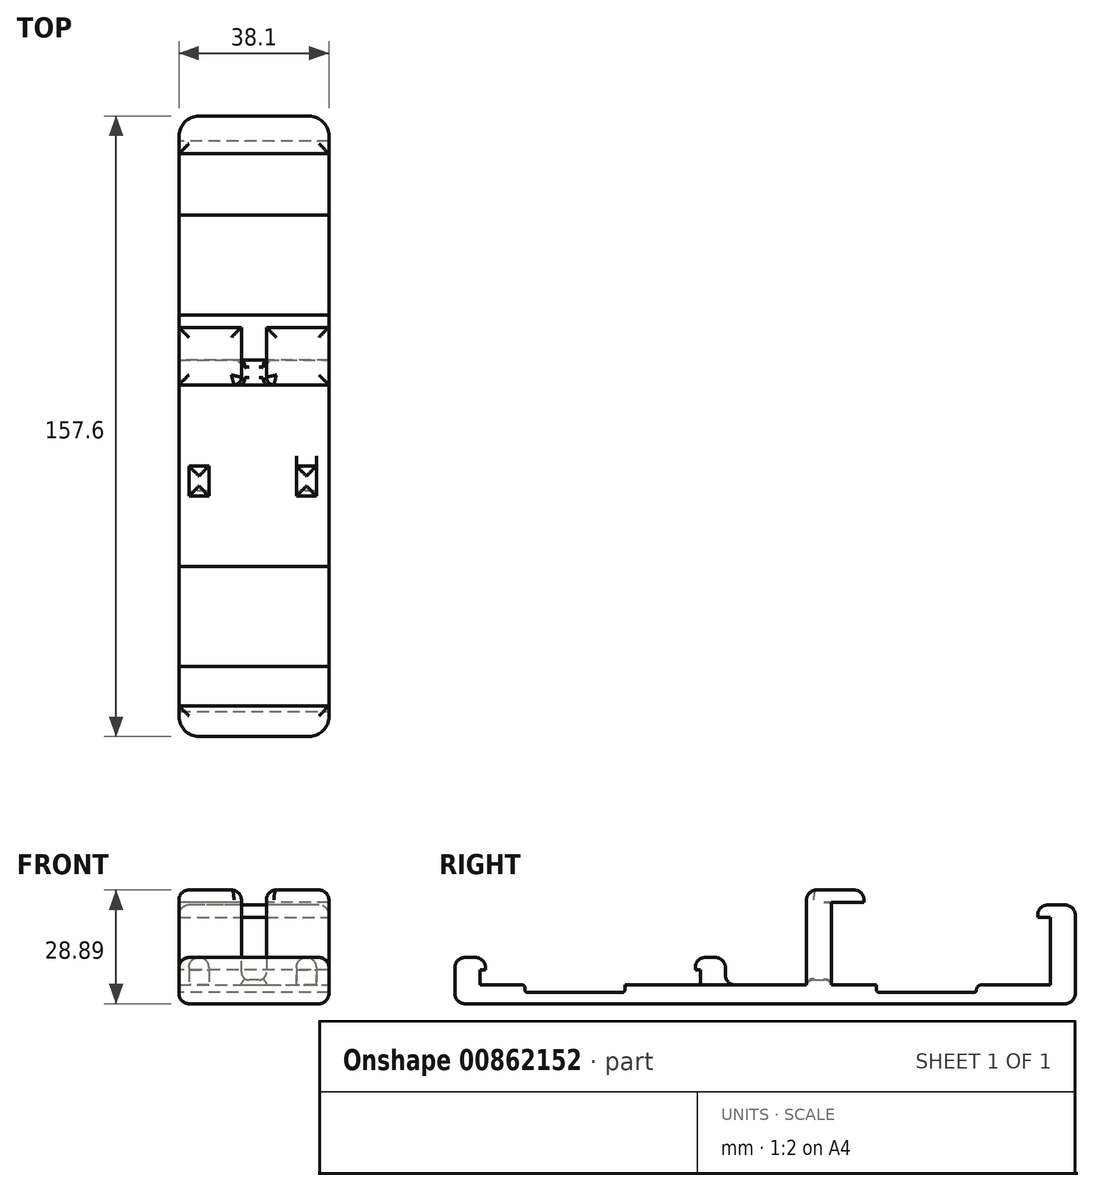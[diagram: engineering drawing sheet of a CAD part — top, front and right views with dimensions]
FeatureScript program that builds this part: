
annotation { "Feature Type Name" : "Feature", "Feature Type Description" : "" }
export const myFeature = defineFeature(function(context is Context, id is Id, definition is map)
    precondition{}
    {
        {
            var Q0;
            Q0=qCreatedBy(makeId("Top.planeOp"),FACE);
            var sketch = newSketch(context, id + "F0", { "sketchPlane" : qUnion([Q0])});
            skLineSegment(sketch, "E0.bottom", {"start": v(0, 0) * mm, "end": v(88, 0) * mm, "construction": true});
            skLineSegment(sketch, "E0.top", {"start": v(0, 56) * mm, "end": v(88, 56) * mm, "construction": true});
            skLineSegment(sketch, "E0.left", {"start": v(0, 0) * mm, "end": v(0, 56) * mm, "construction": true});
            skLineSegment(sketch, "E0.right", {"start": v(88, 0) * mm, "end": v(88, 56) * mm, "construction": true});
            skLineSegment(sketch, "E1.bottom", {"start": v(12.26, -6.35) * mm, "end": v(50.36, -6.35) * mm});
            skLineSegment(sketch, "E1.top", {"start": v(12.26, 62.35) * mm, "end": v(50.36, 62.35) * mm});
            skLineSegment(sketch, "E1.left", {"start": v(12.26, -6.35) * mm, "end": v(12.26, 62.35) * mm});
            skLineSegment(sketch, "E1.right", {"start": v(50.36, -6.35) * mm, "end": v(50.36, 62.35) * mm});
            skSolve(sketch);
        }
        {
            var Q0;
            Q0 = qSketchRegion(id + "F0", true);
            extrude(context, id + "F1", {"entities" : qUnion([Q0]), "depth" : 4.76 * mm, "offsetDistance" : 25.4 * mm});
        }
        {
            var Q0;
            Q0=makeQuery(id+"F1.opExtrude","CAP_FACE",FACE,{"disambiguationData":[OSD([sQuery(id+"F0.wireOp",EDGE,"E1.bottom"),sQuery(id+"F0.wireOp",EDGE,"E1.top"),sQuery(id+"F0.wireOp",EDGE,"E1.left"),sQuery(id+"F0.wireOp",EDGE,"E1.right")])],"isStart":false});
            var sketch = newSketch(context, id + "F2", { "sketchPlane" : qUnion([Q0])});
            skLineSegment(sketch, "E2.bottom", {"start": v(12.26, -6.35) * mm, "end": v(50.36, -6.35) * mm});
            skLineSegment(sketch, "E2.top", {"start": v(12.26, 0) * mm, "end": v(50.36, 0) * mm});
            skLineSegment(sketch, "E2.left", {"start": v(12.26, -6.35) * mm, "end": v(12.26, 0) * mm});
            skLineSegment(sketch, "E2.right", {"start": v(50.36, -6.35) * mm, "end": v(50.36, 0) * mm});
            skLineSegment(sketch, "E3.bottom", {"start": v(19.88, 56) * mm, "end": v(14.8, 56) * mm});
            skLineSegment(sketch, "E3.top", {"start": v(19.88, 62.35) * mm, "end": v(14.8, 62.35) * mm});
            skLineSegment(sketch, "E3.left", {"start": v(19.88, 56) * mm, "end": v(19.88, 62.35) * mm});
            skLineSegment(sketch, "E3.right", {"start": v(14.8, 56) * mm, "end": v(14.8, 62.35) * mm});
            skLineSegment(sketch, "E4.1.0.0", {"start": v(47.18, 56) * mm, "end": v(42.1, 56) * mm});
            skLineSegment(sketch, "E4.1.0.1", {"start": v(42.1, 56) * mm, "end": v(42.1, 62.35) * mm});
            skLineSegment(sketch, "E4.1.0.2", {"start": v(47.18, 56) * mm, "end": v(47.18, 62.35) * mm});
            skLineSegment(sketch, "E4.1.0.3", {"start": v(47.18, 62.35) * mm, "end": v(42.1, 62.35) * mm});
            skLineSegment(sketch, "E4.direction1", {"start": v(14.8, 56) * mm, "end": v(42.1, 56) * mm, "construction": true});
            skSolve(sketch);
        }
        {
            var Q0;
            Q0 = qSketchRegion(id + "F2", true);
            extrude(context, id + "F3", {"entities" : qUnion([Q0]), "operationType" : NewBodyOperationType.ADD, "depth" : 7 * mm, "offsetDistance" : 25.4 * mm});
        }
        {
            var Q0;
            Q0=makeQuery(id+"F3.opExtrude","SWEPT_FACE",FACE,{"disambiguationData":[OSD([sQuery(id+"F2.wireOp",EDGE,"E3.bottom")])]});
            var sketch = newSketch(context, id + "F4", { "sketchPlane" : qUnion([Q0])});
            skLineSegment(sketch, "E5.bottom", {"start": v(12.26, 11.75) * mm, "end": v(46.53, 11.75) * mm, "construction": true});
            skLineSegment(sketch, "E5.top", {"start": v(12.26, 8.57) * mm, "end": v(46.53, 8.57) * mm, "construction": true});
            skLineSegment(sketch, "E5.left", {"start": v(12.26, 11.75) * mm, "end": v(12.26, 8.57) * mm, "construction": true});
            skLineSegment(sketch, "E5.right", {"start": v(46.53, 11.75) * mm, "end": v(46.53, 8.57) * mm, "construction": true});
            skLineSegment(sketch, "E6.bottom", {"start": v(14.8, 11.75) * mm, "end": v(19.88, 11.75) * mm});
            skLineSegment(sketch, "E6.top", {"start": v(14.8, 8.57) * mm, "end": v(19.88, 8.57) * mm});
            skLineSegment(sketch, "E6.left", {"start": v(14.8, 11.75) * mm, "end": v(14.8, 8.57) * mm});
            skLineSegment(sketch, "E6.right", {"start": v(19.88, 11.75) * mm, "end": v(19.88, 8.57) * mm});
            skLineSegment(sketch, "E7.1.0.0", {"start": v(42.1, 11.75) * mm, "end": v(42.1, 8.57) * mm});
            skLineSegment(sketch, "E7.1.0.1", {"start": v(39.56, 11.75) * mm, "end": v(73.84, 11.75) * mm, "construction": true});
            skLineSegment(sketch, "E7.1.0.2", {"start": v(39.56, 11.75) * mm, "end": v(39.56, 8.57) * mm, "construction": true});
            skLineSegment(sketch, "E7.1.0.3", {"start": v(39.56, 8.57) * mm, "end": v(73.84, 8.57) * mm, "construction": true});
            skLineSegment(sketch, "E7.1.0.4", {"start": v(47.18, 11.75) * mm, "end": v(47.18, 8.57) * mm});
            skLineSegment(sketch, "E7.1.0.5", {"start": v(42.1, 8.57) * mm, "end": v(47.18, 8.57) * mm});
            skLineSegment(sketch, "E7.1.0.6", {"start": v(42.1, 11.75) * mm, "end": v(47.18, 11.75) * mm});
            skLineSegment(sketch, "E7.direction1", {"start": v(12.26, 8.57) * mm, "end": v(39.56, 8.57) * mm, "construction": true});
            skSolve(sketch);
        }
        {
            var Q0;
            Q0 = qSketchRegion(id + "F4", true);
            extrude(context, id + "F5", {"entities" : qUnion([Q0]), "operationType" : NewBodyOperationType.ADD, "depth" : 1.27 * mm, "offsetDistance" : 25.4 * mm});
        }
        {
            var Q0;
            Q0=makeQuery(id+"F3.opExtrude","SWEPT_FACE",FACE,{"disambiguationData":[OSD([sQuery(id+"F2.wireOp",EDGE,"E2.top")])]});
            var sketch = newSketch(context, id + "F6", { "sketchPlane" : qUnion([Q0])});
            skLineSegment(sketch, "E8.bottom", {"start": v(-50.36, 11.75) * mm, "end": v(-12.26, 11.75) * mm});
            skLineSegment(sketch, "E8.top", {"start": v(-50.36, 8.57) * mm, "end": v(-12.26, 8.57) * mm});
            skLineSegment(sketch, "E8.left", {"start": v(-50.36, 11.75) * mm, "end": v(-50.36, 8.57) * mm});
            skLineSegment(sketch, "E8.right", {"start": v(-12.26, 11.75) * mm, "end": v(-12.26, 8.57) * mm});
            skSolve(sketch);
        }
        {
            var Q0;
            Q0 = qSketchRegion(id + "F6", true);
            extrude(context, id + "F7", {"entities" : qUnion([Q0]), "operationType" : NewBodyOperationType.ADD, "depth" : 1.4 * mm, "offsetDistance" : 25.4 * mm});
        }
        {
            var Q0;
            Q0=makeQuery(id+"F3.boolean.opBoolean","MERGE",FACE,{"derivedFrom":[makeQuery(id+"F1.opExtrude","SWEPT_FACE",FACE,{"disambiguationData":[OSD([sQuery(id+"F0.wireOp",EDGE,"E1.top")])]}),makeQuery(id+"F3.opExtrude","SWEPT_FACE",FACE,{"disambiguationData":[OSD([sQuery(id+"F2.wireOp",EDGE,"bA279OWE-RNau-AAjO-aDuQ-ZZpBOvPAffWd.bottom")])]})]});
            var sketch = newSketch(context, id + "F8", { "sketchPlane" : qUnion([Q0])});
            skLineSegment(sketch, "E9.bottom", {"start": v(-50.36, 0) * mm, "end": v(-12.26, 0) * mm});
            skLineSegment(sketch, "E9.top", {"start": v(-50.36, 4.76) * mm, "end": v(-12.26, 4.76) * mm});
            skLineSegment(sketch, "E9.left", {"start": v(-50.36, 0) * mm, "end": v(-50.36, 4.76) * mm});
            skLineSegment(sketch, "E9.right", {"start": v(-12.26, 0) * mm, "end": v(-12.26, 4.76) * mm});
            skSolve(sketch);
        }
        {
            var Q0;
            Q0 = qSketchRegion(id + "F8", true);
            extrude(context, id + "F9", {"entities" : qUnion([Q0]), "operationType" : NewBodyOperationType.ADD, "depth" : 88.9 * mm, "offsetDistance" : 25.4 * mm});
        }
        {
            var Q0;
            Q0=makeQuery(id+"F9.opExtrude","SWEPT_FACE",FACE,{"disambiguationData":[OSD([sQuery(id+"F8.wireOp",EDGE,"E9.top")])]});
            var sketch = newSketch(context, id + "F10", { "sketchPlane" : qUnion([Q0])});
            skLineSegment(sketch, "E10.bottom", {"start": v(12.26, 89.34) * mm, "end": v(50.36, 89.34) * mm});
            skLineSegment(sketch, "E10.top", {"start": v(12.26, 82.99) * mm, "end": v(50.36, 82.99) * mm});
            skLineSegment(sketch, "E10.left", {"start": v(12.26, 89.34) * mm, "end": v(12.26, 82.99) * mm});
            skLineSegment(sketch, "E10.right", {"start": v(50.36, 89.34) * mm, "end": v(50.36, 82.99) * mm});
            skSolve(sketch);
        }
        {
            var Q0;
            Q0 = qSketchRegion(id + "F10", true);
            extrude(context, id + "F11", {"entities" : qUnion([Q0]), "operationType" : NewBodyOperationType.ADD, "depth" : 24.13 * mm, "offsetDistance" : 25.4 * mm});
        }
        {
            var Q0;
            {var subQ1=sQuery(id+"F10.wireOp",EDGE,"E10.bottom");Q0=makeQuery(id+"F15.boolean.opBoolean","SPLIT",FACE,{"disambiguationData":[TD([makeQuery(id+"F1.opExtrude","SWEPT_FACE",FACE,{"disambiguationData":[OSD([sQuery(id+"F0.wireOp",EDGE,"E1.right")])]})])],"derivedFrom":makeQuery(id+"F11.opExtrude","SWEPT_FACE",FACE,{"disambiguationData":[OSD([subQ1])]})});}
            var sketch = newSketch(context, id + "F12", { "sketchPlane" : qUnion([Q0])});
            skLineSegment(sketch, "E11.bottom", {"start": v(-50.36, 28.9) * mm, "end": v(-12.26, 28.9) * mm});
            skLineSegment(sketch, "E11.top", {"start": v(-50.36, 25.72) * mm, "end": v(-12.26, 25.72) * mm});
            skLineSegment(sketch, "E11.left", {"start": v(-50.36, 28.9) * mm, "end": v(-50.36, 25.72) * mm});
            skLineSegment(sketch, "E11.right", {"start": v(-12.26, 28.9) * mm, "end": v(-12.26, 25.72) * mm});
            skSolve(sketch);
        }
        {
            var Q0;
            Q0=makeQuery(id+"F11.opExtrude","CAP_FACE",FACE,{"disambiguationData":[OSD([sQuery(id+"F10.wireOp",EDGE,"E10.bottom"),sQuery(id+"F10.wireOp",EDGE,"E10.top"),sQuery(id+"F10.wireOp",EDGE,"E10.left"),sQuery(id+"F10.wireOp",EDGE,"E10.right")])],"isStart":false});
            var sketch = newSketch(context, id + "F13", { "sketchPlane" : qUnion([Q0])});
            skLineSegment(sketch, "E12.bottom", {"start": v(34.48, 99.5) * mm, "end": v(28.13, 99.5) * mm});
            skLineSegment(sketch, "E12.top", {"start": v(51.97, 74.1) * mm, "end": v(28.13, 74.1) * mm});
            skLineSegment(sketch, "E13", {"start": v(28.13, 99.5) * mm, "end": v(28.13, 74.1) * mm});
            skLineSegment(sketch, "E14", {"start": v(51.97, 74.1) * mm, "end": v(51.97, 80.45) * mm});
            skLineSegment(sketch, "E15", {"start": v(51.97, 80.45) * mm, "end": v(34.48, 80.45) * mm});
            skLineSegment(sketch, "E16", {"start": v(34.48, 80.45) * mm, "end": v(34.48, 99.5) * mm});
            skSolve(sketch);
        }
        {
            var Q0;
            Q0 = qSketchRegion(id + "F12", true);
            extrude(context, id + "F14", {"entities" : qUnion([Q0]), "operationType" : NewBodyOperationType.ADD, "depth" : 8.25 * mm, "offsetDistance" : 25.4 * mm});
        }
        {
            var Q0;
            {var subQ0=sQuery(id+"F13.wireOp",EDGE,"E13");var subQ1=makeQuery(id+"F11.opExtrude","CAP_EDGE",EDGE,{"disambiguationData":[OSD([sQuery(id+"F10.wireOp",EDGE,"E10.bottom")])],"isStart":false});var subQ2=makeQuery(id+"F13.imprint","INTERSECT",VERTEX,{"derivedFrom":[subQ1,subQ0]});Q0=makeQuery(id+"F13.imprint","IMPRINT",FACE,{"disambiguationData":[TD([[makeQuery(id+"F13.imprint","IMPRINT",EDGE,{"disambiguationData":[TD([[subQ2,-1.0]])],"derivedFrom":subQ0}),1.0]])]});}
            var Q1;
            {var subQ0=sQuery(id+"F13.wireOp",EDGE,"E12.bottom");Q1=makeQuery(id+"F13.imprint","IMPRINT",FACE,{"disambiguationData":[TD([[makeQuery(id+"F13.imprint","IMPRINT",EDGE,{"derivedFrom":subQ0}),1.0]])]});}
            var Q2;
            {var subQ1=sQuery(id+"F13.wireOp",EDGE,"E12.top");Q2=makeQuery(id+"F13.imprint","IMPRINT",FACE,{"disambiguationData":[TD([[makeQuery(id+"F13.imprint","IMPRINT",EDGE,{"derivedFrom":subQ1}),-1.0]])]});}
            extrude(context, id + "F15", {"entities" : qUnion([Q0, Q1, Q2]), "operationType" : NewBodyOperationType.REMOVE, "oppositeDirection" : true, "depth" : 22.86 * mm, "offsetDistance" : 25.4 * mm});
        }
        {
            var Q0;
            {var subQ0=sQuery(id+"F8.wireOp",EDGE,"E9.left");var subQ3=sQuery(id+"F8.wireOp",EDGE,"E9.top");Q0=makeQuery(id+"F22.boolean.opBoolean","SPLIT",FACE,{"disambiguationData":[TD([makeQuery(id+"F24.opFillet","BLEND_FACE",FACE,{"disambiguationData":[OSD([subQ0])]})])],"derivedFrom":makeQuery(id+"F11.boolean.opBoolean","SPLIT",FACE,{"disambiguationData":[TD([makeQuery(id+"F11.opExtrude","SWEPT_FACE",FACE,{"disambiguationData":[OSD([sQuery(id+"F10.wireOp",EDGE,"E10.bottom")])]})])],"derivedFrom":makeQuery(id+"F9.opExtrude","SWEPT_FACE",FACE,{"disambiguationData":[OSD([subQ3])]})})});}
            var sketch = newSketch(context, id + "F16", { "sketchPlane" : qUnion([Q0])});
            skLineSegment(sketch, "E17.bottom", {"start": v(50.36, 144.9) * mm, "end": v(12.26, 144.9) * mm});
            skLineSegment(sketch, "E17.top", {"start": v(50.36, 151.25) * mm, "end": v(12.26, 151.25) * mm});
            skLineSegment(sketch, "E17.left", {"start": v(50.36, 144.9) * mm, "end": v(50.36, 151.25) * mm});
            skLineSegment(sketch, "E17.right", {"start": v(12.26, 144.9) * mm, "end": v(12.26, 151.25) * mm});
            skSolve(sketch);
        }
        {
            var Q0;
            Q0 = qSketchRegion(id + "F16", true);
            extrude(context, id + "F17", {"entities" : qUnion([Q0]), "operationType" : NewBodyOperationType.ADD, "depth" : 20.32 * mm, "offsetDistance" : 25.4 * mm});
        }
        {
            var Q0;
            Q0=makeQuery(id+"F17.opExtrude","SWEPT_FACE",FACE,{"disambiguationData":[OSD([sQuery(id+"F16.wireOp",EDGE,"E17.bottom")])]});
            var sketch = newSketch(context, id + "F18", { "sketchPlane" : qUnion([Q0])});
            skLineSegment(sketch, "E18.bottom", {"start": v(12.26, 25.08) * mm, "end": v(50.36, 25.08) * mm});
            skLineSegment(sketch, "E18.top", {"start": v(12.26, 21.9) * mm, "end": v(50.36, 21.9) * mm});
            skLineSegment(sketch, "E18.left", {"start": v(12.26, 25.08) * mm, "end": v(12.26, 21.9) * mm});
            skLineSegment(sketch, "E18.right", {"start": v(50.36, 25.08) * mm, "end": v(50.36, 21.9) * mm});
            skSolve(sketch);
        }
        {
            var Q0;
            Q0 = qSketchRegion(id + "F18", true);
            extrude(context, id + "F19", {"entities" : qUnion([Q0]), "operationType" : NewBodyOperationType.ADD, "depth" : 3.17 * mm, "offsetDistance" : 25.4 * mm});
        }
        {
            var Q0;
            Q0=makeQuery(id+"F7.boolean.opBoolean","MERGE",FACE,{"derivedFrom":[makeQuery(id+"F3.opExtrude","CAP_FACE",FACE,{"disambiguationData":[OSD([sQuery(id+"F2.wireOp",EDGE,"E2.bottom"),sQuery(id+"F2.wireOp",EDGE,"E2.top"),sQuery(id+"F2.wireOp",EDGE,"E2.left"),sQuery(id+"F2.wireOp",EDGE,"E2.right")])],"isStart":false}),makeQuery(id+"F7.opExtrude","SWEPT_FACE",FACE,{"disambiguationData":[OSD([sQuery(id+"F6.wireOp",EDGE,"E8.bottom")])]})]});
            var Q1;
            Q1=makeQuery(id+"F5.boolean.opBoolean","MERGE",FACE,{"derivedFrom":[makeQuery(id+"F3.opExtrude","CAP_FACE",FACE,{"disambiguationData":[OSD([sQuery(id+"F2.wireOp",EDGE,"bA279OWE-RNau-AAjO-aDuQ-ZZpBOvPAffWd.bottom"),sQuery(id+"F2.wireOp",EDGE,"bA279OWE-RNau-AAjO-aDuQ-ZZpBOvPAffWd.top"),sQuery(id+"F2.wireOp",EDGE,"bA279OWE-RNau-AAjO-aDuQ-ZZpBOvPAffWd.left"),sQuery(id+"F2.wireOp",EDGE,"bA279OWE-RNau-AAjO-aDuQ-ZZpBOvPAffWd.right")])],"isStart":false}),makeQuery(id+"F5.opExtrude","SWEPT_FACE",FACE,{"disambiguationData":[OSD([sQuery(id+"F4.wireOp",EDGE,"E5.bottom")])]})]});
            var Q2;
            {var subQ1=sQuery(id+"F12.wireOp",EDGE,"E11.bottom");var subQ2=sQuery(id+"F10.wireOp",EDGE,"E10.left");var subQ3=sQuery(id+"F10.wireOp",EDGE,"E10.top");Q2=makeQuery(id+"F15.boolean.opBoolean","SPLIT",FACE,{"disambiguationData":[TD([makeQuery(id+"F1.opExtrude","SWEPT_FACE",FACE,{"disambiguationData":[OSD([sQuery(id+"F0.wireOp",EDGE,"E1.left")])]})])],"derivedFrom":makeQuery(id+"F14.boolean.opBoolean","MERGE",FACE,{"derivedFrom":[makeQuery(id+"F11.opExtrude","CAP_FACE",FACE,{"disambiguationData":[OSD([sQuery(id+"F10.wireOp",EDGE,"E10.bottom"),subQ3,subQ2,sQuery(id+"F10.wireOp",EDGE,"E10.right")])],"isStart":false}),makeQuery(id+"F14.opExtrude","SWEPT_FACE",FACE,{"disambiguationData":[OSD([subQ1])]})]})});}
            var Q3;
            {var subQ0=sQuery(id+"F10.wireOp",EDGE,"E10.right");var subQ1=sQuery(id+"F10.wireOp",EDGE,"E10.top");var subQ3=sQuery(id+"F12.wireOp",EDGE,"E11.bottom");Q3=makeQuery(id+"F15.boolean.opBoolean","SPLIT",FACE,{"disambiguationData":[TD([makeQuery(id+"F1.opExtrude","SWEPT_FACE",FACE,{"disambiguationData":[OSD([sQuery(id+"F0.wireOp",EDGE,"E1.right")])]})])],"derivedFrom":makeQuery(id+"F14.boolean.opBoolean","MERGE",FACE,{"derivedFrom":[makeQuery(id+"F11.opExtrude","CAP_FACE",FACE,{"disambiguationData":[OSD([sQuery(id+"F10.wireOp",EDGE,"E10.bottom"),subQ1,sQuery(id+"F10.wireOp",EDGE,"E10.left"),subQ0])],"isStart":false}),makeQuery(id+"F14.opExtrude","SWEPT_FACE",FACE,{"disambiguationData":[OSD([subQ3])]})]})});}
            var Q4;
            Q4=makeQuery(id+"F9.boolean.opBoolean","MERGE",FACE,{"derivedFrom":[makeQuery(id+"F1.opExtrude","CAP_FACE",FACE,{"disambiguationData":[OSD([sQuery(id+"F0.wireOp",EDGE,"E1.bottom"),sQuery(id+"F0.wireOp",EDGE,"E1.top"),sQuery(id+"F0.wireOp",EDGE,"E1.left"),sQuery(id+"F0.wireOp",EDGE,"E1.right")])],"isStart":true}),makeQuery(id+"F9.opExtrude","SWEPT_FACE",FACE,{"disambiguationData":[OSD([sQuery(id+"F8.wireOp",EDGE,"E9.bottom")])]})]});
            var Q5;
            Q5=makeQuery(id+"F15.boolean.opBoolean","COPY",EDGE,{"derivedFrom":makeQuery(id+"F15.opExtrude","SWEPT_EDGE",EDGE,{"disambiguationData":[OSD([sQuery(id+"F13.wireOp",EDGE,"E13"),sQuery(id+"F13.wireOp",EDGE,"QISQvM3N-z2vj-XqKH-QPA1-7KimYQfk3j7Q")])]})});
            var Q6;
            Q6=makeQuery(id+"F15.boolean.opBoolean","COPY",EDGE,{"derivedFrom":makeQuery(id+"F15.opExtrude","SWEPT_EDGE",EDGE,{"disambiguationData":[OSD([sQuery(id+"F13.wireOp",EDGE,"E12.top"),sQuery(id+"F13.wireOp",EDGE,"E12.right")])]})});
            var Q7;
            Q7=makeQuery(id+"F19.boolean.opBoolean","MERGE",FACE,{"derivedFrom":[makeQuery(id+"F11.opExtrude","CAP_FACE",FACE,{"disambiguationData":[OSD([sQuery(id+"F10.wireOp",EDGE,"fdR43w3e-D3ww-igFy-iP3o-ReilXkbukFnq.bottom"),sQuery(id+"F10.wireOp",EDGE,"fdR43w3e-D3ww-igFy-iP3o-ReilXkbukFnq.top"),sQuery(id+"F10.wireOp",EDGE,"fdR43w3e-D3ww-igFy-iP3o-ReilXkbukFnq.left"),sQuery(id+"F10.wireOp",EDGE,"fdR43w3e-D3ww-igFy-iP3o-ReilXkbukFnq.right")])],"isStart":false}),makeQuery(id+"F19.opExtrude","SWEPT_FACE",FACE,{"disambiguationData":[OSD([sQuery(id+"F18.wireOp",EDGE,"Ol4su5Gu-75hp-AgvY-yYLj-UDWePbQuPs0d.bottom")])]})]});
            var Q8;
            Q8=makeQuery(id+"F19.boolean.opBoolean","MERGE",FACE,{"derivedFrom":[makeQuery(id+"F17.opExtrude","CAP_FACE",FACE,{"disambiguationData":[OSD([sQuery(id+"F16.wireOp",EDGE,"E17.bottom"),sQuery(id+"F16.wireOp",EDGE,"E17.top"),sQuery(id+"F16.wireOp",EDGE,"E17.left"),sQuery(id+"F16.wireOp",EDGE,"E17.right")])],"isStart":false}),makeQuery(id+"F19.opExtrude","SWEPT_FACE",FACE,{"disambiguationData":[OSD([sQuery(id+"F18.wireOp",EDGE,"E18.bottom")])]})]});
            var Q9;
            Q9=makeQuery(id+"F5.boolean.opBoolean","MERGE",FACE,{"derivedFrom":[makeQuery(id+"F3.opExtrude","CAP_FACE",FACE,{"disambiguationData":[OSD([sQuery(id+"F2.wireOp",EDGE,"E3.bottom"),sQuery(id+"F2.wireOp",EDGE,"E3.top"),sQuery(id+"F2.wireOp",EDGE,"E3.left"),sQuery(id+"F2.wireOp",EDGE,"E3.right")])],"isStart":false}),makeQuery(id+"F5.opExtrude","SWEPT_FACE",FACE,{"disambiguationData":[OSD([sQuery(id+"F4.wireOp",EDGE,"E6.bottom")])]})]});
            var Q10;
            Q10=makeQuery(id+"F3.opExtrude","CAP_EDGE",EDGE,{"disambiguationData":[OSD([sQuery(id+"F2.wireOp",EDGE,"E3.left")])],"isStart":true});
            var Q11;
            Q11=makeQuery(id+"F3.opExtrude","CAP_EDGE",EDGE,{"disambiguationData":[OSD([sQuery(id+"F2.wireOp",EDGE,"E3.right")])],"isStart":true});
            fillet(context, id + "F20", {"entities" : qUnion([Q0, Q1, Q2, Q3, Q4, Q5, Q6, Q7, Q8, Q9, Q10, Q11]), "radius" : 2.54 * mm, "tangentPropagation" : true, "allowEdgeOverflow" : false});
        }
        {
            var Q0;
            Q0=makeQuery(id+"F1.opExtrude","CAP_FACE",FACE,{"disambiguationData":[OSD([sQuery(id+"F0.wireOp",EDGE,"E1.bottom"),sQuery(id+"F0.wireOp",EDGE,"E1.top"),sQuery(id+"F0.wireOp",EDGE,"E1.left"),sQuery(id+"F0.wireOp",EDGE,"E1.right")])],"isStart":false});
            var sketch = newSketch(context, id + "F21", { "sketchPlane" : qUnion([Q0])});
            skLineSegment(sketch, "E19.bottom", {"start": v(50.36, 11.43) * mm, "end": v(12.26, 11.43) * mm});
            skLineSegment(sketch, "E19.top", {"start": v(50.36, 36.83) * mm, "end": v(12.26, 36.83) * mm});
            skLineSegment(sketch, "E19.left", {"start": v(50.36, 11.43) * mm, "end": v(50.36, 36.83) * mm});
            skLineSegment(sketch, "E19.right", {"start": v(12.26, 11.43) * mm, "end": v(12.26, 36.83) * mm});
            skLineSegment(sketch, "E20.bottom", {"start": v(10.98, 126.17) * mm, "end": v(79.85, 126.17) * mm});
            skLineSegment(sketch, "E20.top", {"start": v(10.98, 100.77) * mm, "end": v(79.85, 100.77) * mm});
            skLineSegment(sketch, "E20.left", {"start": v(10.98, 126.17) * mm, "end": v(10.98, 100.77) * mm});
            skLineSegment(sketch, "E20.right", {"start": v(79.85, 126.17) * mm, "end": v(79.85, 100.77) * mm});
            skSolve(sketch);
        }
        {
            var Q0;
            Q0 = qSketchRegion(id + "F21", true);
            extrude(context, id + "F22", {"entities" : qUnion([Q0]), "operationType" : NewBodyOperationType.REMOVE, "oppositeDirection" : true, "depth" : 1.9 * mm, "offsetDistance" : 25.4 * mm});
        }
        {
            var Q0;
            Q0=makeQuery(id+"F22.boolean.opBoolean","COPY",EDGE,{"derivedFrom":makeQuery(id+"F22.opExtrude","CAP_EDGE",EDGE,{"disambiguationData":[OSD([sQuery(id+"F21.wireOp",EDGE,"E19.top")])],"isStart":true})});
            var Q1;
            Q1=makeQuery(id+"F22.boolean.opBoolean","COPY",EDGE,{"derivedFrom":makeQuery(id+"F22.opExtrude","CAP_EDGE",EDGE,{"disambiguationData":[OSD([sQuery(id+"F21.wireOp",EDGE,"E19.bottom")])],"isStart":true})});
            var Q2;
            Q2=makeQuery(id+"F22.boolean.opBoolean","INTERSECT",EDGE,{"derivedFrom":[makeQuery(id+"F11.boolean.opBoolean","SPLIT",FACE,{"disambiguationData":[TD([makeQuery(id+"F11.opExtrude","SWEPT_FACE",FACE,{"disambiguationData":[OSD([sQuery(id+"F10.wireOp",EDGE,"fdR43w3e-D3ww-igFy-iP3o-ReilXkbukFnq.top")])]})])],"derivedFrom":makeQuery(id+"F9.opExtrude","SWEPT_FACE",FACE,{"disambiguationData":[OSD([sQuery(id+"F8.wireOp",EDGE,"E9.top")])]})}),makeQuery(id+"F22.opExtrude","SWEPT_FACE",FACE,{"disambiguationData":[OSD([sQuery(id+"F21.wireOp",EDGE,"E20.top")])]})]});
            var Q3;
            Q3=makeQuery(id+"F22.boolean.opBoolean","INTERSECT",EDGE,{"derivedFrom":[makeQuery(id+"F11.boolean.opBoolean","SPLIT",FACE,{"disambiguationData":[TD([makeQuery(id+"F11.opExtrude","SWEPT_FACE",FACE,{"disambiguationData":[OSD([sQuery(id+"F10.wireOp",EDGE,"fdR43w3e-D3ww-igFy-iP3o-ReilXkbukFnq.top")])]})])],"derivedFrom":makeQuery(id+"F9.opExtrude","SWEPT_FACE",FACE,{"disambiguationData":[OSD([sQuery(id+"F8.wireOp",EDGE,"E9.top")])]})}),makeQuery(id+"F22.opExtrude","SWEPT_FACE",FACE,{"disambiguationData":[OSD([sQuery(id+"F21.wireOp",EDGE,"E20.bottom")])]})]});
            var Q4;
            Q4=makeQuery(id+"F22.boolean.opBoolean","COPY",EDGE,{"derivedFrom":makeQuery(id+"F22.opExtrude","CAP_EDGE",EDGE,{"disambiguationData":[OSD([sQuery(id+"F21.wireOp",EDGE,"E19.top")])],"isStart":false})});
            var Q5;
            Q5=makeQuery(id+"F22.boolean.opBoolean","COPY",EDGE,{"derivedFrom":makeQuery(id+"F22.opExtrude","CAP_EDGE",EDGE,{"disambiguationData":[OSD([sQuery(id+"F21.wireOp",EDGE,"E19.bottom")])],"isStart":false})});
            var Q6;
            Q6=makeQuery(id+"F22.boolean.opBoolean","COPY",EDGE,{"derivedFrom":makeQuery(id+"F22.opExtrude","CAP_EDGE",EDGE,{"disambiguationData":[OSD([sQuery(id+"F21.wireOp",EDGE,"E20.top")])],"isStart":false})});
            var Q7;
            Q7=makeQuery(id+"F22.boolean.opBoolean","COPY",EDGE,{"derivedFrom":makeQuery(id+"F22.opExtrude","CAP_EDGE",EDGE,{"disambiguationData":[OSD([sQuery(id+"F21.wireOp",EDGE,"E20.bottom")])],"isStart":false})});
            fillet(context, id + "F23", {"entities" : qUnion([Q0, Q1, Q2, Q3, Q4, Q5, Q6, Q7]), "radius" : 0.64 * mm, "allowEdgeOverflow" : false});
        }
        {
            var Q0;
            Q0=makeQuery(id+"F11.boolean.opBoolean","MERGE",EDGE,{"derivedFrom":[makeQuery(id+"F9.opExtrude","CAP_EDGE",EDGE,{"disambiguationData":[OSD([sQuery(id+"F8.wireOp",EDGE,"E9.left")])],"isStart":false}),makeQuery(id+"F11.opExtrude","SWEPT_EDGE",EDGE,{"disambiguationData":[OSD([sQuery(id+"F10.wireOp",EDGE,"fdR43w3e-D3ww-igFy-iP3o-ReilXkbukFnq.bottom"),sQuery(id+"F10.wireOp",EDGE,"fdR43w3e-D3ww-igFy-iP3o-ReilXkbukFnq.left")])]})]});
            var Q1;
            Q1=makeQuery(id+"F11.boolean.opBoolean","MERGE",EDGE,{"derivedFrom":[makeQuery(id+"F9.opExtrude","CAP_EDGE",EDGE,{"disambiguationData":[OSD([sQuery(id+"F8.wireOp",EDGE,"E9.right")])],"isStart":false}),makeQuery(id+"F11.opExtrude","SWEPT_EDGE",EDGE,{"disambiguationData":[OSD([sQuery(id+"F10.wireOp",EDGE,"fdR43w3e-D3ww-igFy-iP3o-ReilXkbukFnq.bottom"),sQuery(id+"F10.wireOp",EDGE,"fdR43w3e-D3ww-igFy-iP3o-ReilXkbukFnq.right")])]})]});
            var Q2;
            Q2=makeQuery(id+"F3.boolean.opBoolean","MERGE",EDGE,{"derivedFrom":[makeQuery(id+"F1.opExtrude","SWEPT_EDGE",EDGE,{"disambiguationData":[OSD([sQuery(id+"F0.wireOp",EDGE,"E1.bottom"),sQuery(id+"F0.wireOp",EDGE,"E1.right")])]}),makeQuery(id+"F3.opExtrude","SWEPT_EDGE",EDGE,{"disambiguationData":[OSD([sQuery(id+"F2.wireOp",EDGE,"E2.bottom"),sQuery(id+"F2.wireOp",EDGE,"E2.right")])]})]});
            var Q3;
            Q3=makeQuery(id+"F3.boolean.opBoolean","MERGE",EDGE,{"derivedFrom":[makeQuery(id+"F1.opExtrude","SWEPT_EDGE",EDGE,{"disambiguationData":[OSD([sQuery(id+"F0.wireOp",EDGE,"E1.bottom"),sQuery(id+"F0.wireOp",EDGE,"E1.left")])]}),makeQuery(id+"F3.opExtrude","SWEPT_EDGE",EDGE,{"disambiguationData":[OSD([sQuery(id+"F2.wireOp",EDGE,"E2.bottom"),sQuery(id+"F2.wireOp",EDGE,"E2.left")])]})]});
            fillet(context, id + "F24", {"entities" : qUnion([Q0, Q1, Q2, Q3]), "radius" : 5.08 * mm, "tangentPropagation" : true, "allowEdgeOverflow" : false});
        }
        {
            var Q0;
            Q0=makeQuery(id+"F15.boolean.opBoolean","COPY",EDGE,{"derivedFrom":makeQuery(id+"F15.opExtrude","CAP_EDGE",EDGE,{"disambiguationData":[OSD([sQuery(id+"F13.wireOp",EDGE,"E13")])],"isStart":false})});
            var Q1;
            Q1=makeQuery(id+"F15.boolean.opBoolean","COPY",EDGE,{"derivedFrom":makeQuery(id+"F15.opExtrude","CAP_EDGE",EDGE,{"disambiguationData":[OSD([sQuery(id+"F13.wireOp",EDGE,"E16")])],"isStart":false})});
            fillet(context, id + "F25", {"entities" : qUnion([Q0, Q1]), "radius" : 1.9 * mm, "tangentPropagation" : true, "allowEdgeOverflow" : false});
        }
        {
            var Q0;
            Q0=makeQuery(id+"F15.boolean.opBoolean","INTERSECT",EDGE,{"derivedFrom":[makeQuery(id+"F11.opExtrude","SWEPT_FACE",FACE,{"disambiguationData":[OSD([sQuery(id+"F10.wireOp",EDGE,"E10.top")])]}),makeQuery(id+"F15.opExtrude","SWEPT_FACE",FACE,{"disambiguationData":[OSD([sQuery(id+"F13.wireOp",EDGE,"E16")])]})]});
            var Q1;
            Q1=makeQuery(id+"F15.boolean.opBoolean","INTERSECT",EDGE,{"derivedFrom":[makeQuery(id+"F11.opExtrude","SWEPT_FACE",FACE,{"disambiguationData":[OSD([sQuery(id+"F10.wireOp",EDGE,"E10.bottom")])]}),makeQuery(id+"F15.opExtrude","SWEPT_FACE",FACE,{"disambiguationData":[OSD([sQuery(id+"F13.wireOp",EDGE,"E16")])]})]});
            fillet(context, id + "F26", {"entities" : qUnion([Q0, Q1]), "radius" : 1.9 * mm, "tangentPropagation" : true, "allowEdgeOverflow" : false});
        }
        {
            var Q0;
            Q0=makeQuery(id+"F22.boolean.opBoolean","COPY",EDGE,{"derivedFrom":makeQuery(id+"F22.opExtrude","CAP_EDGE",EDGE,{"disambiguationData":[OSD([sQuery(id+"F21.wireOp",EDGE,"E20.top")])],"isStart":true})});
            var Q1;
            Q1=makeQuery(id+"F11.opExtrude","CAP_EDGE",EDGE,{"disambiguationData":[OSD([sQuery(id+"F10.wireOp",EDGE,"E10.top")])],"isStart":true});
            var Q2;
            Q2=makeQuery(id+"F17.opExtrude","CAP_EDGE",EDGE,{"disambiguationData":[OSD([sQuery(id+"F16.wireOp",EDGE,"E17.bottom")])],"isStart":true});
            var Q3;
            Q3=makeQuery(id+"F22.boolean.opBoolean","COPY",EDGE,{"derivedFrom":makeQuery(id+"F22.opExtrude","CAP_EDGE",EDGE,{"disambiguationData":[OSD([sQuery(id+"F21.wireOp",EDGE,"E20.bottom")])],"isStart":true})});
            fillet(context, id + "F27", {"entities" : qUnion([Q0, Q1, Q2, Q3]), "radius" : 1.27 * mm, "tangentPropagation" : true, "allowEdgeOverflow" : false});
        }
        {
            var Q0;
            Q0=makeQuery(id+"F3.opExtrude","CAP_EDGE",EDGE,{"disambiguationData":[OSD([sQuery(id+"F2.wireOp",EDGE,"E4.1.0.3")])],"isStart":false});
            var Q1;
            Q1=makeQuery(id+"F3.opExtrude","CAP_EDGE",EDGE,{"disambiguationData":[OSD([sQuery(id+"F2.wireOp",EDGE,"E4.1.0.2")])],"isStart":false});
            var Q2;
            Q2=makeQuery(id+"F5.opExtrude","CAP_EDGE",EDGE,{"disambiguationData":[OSD([sQuery(id+"F4.wireOp",EDGE,"E7.1.0.6")])],"isStart":false});
            var Q3;
            Q3=makeQuery(id+"F3.opExtrude","CAP_EDGE",EDGE,{"disambiguationData":[OSD([sQuery(id+"F2.wireOp",EDGE,"E4.1.0.1")])],"isStart":false});
            var Q4;
            Q4=makeQuery(id+"F3.opExtrude","CAP_EDGE",EDGE,{"disambiguationData":[OSD([sQuery(id+"F2.wireOp",EDGE,"E4.1.0.1")])],"isStart":true});
            var Q5;
            {var subQ0=sQuery(id+"F8.wireOp",EDGE,"E9.top");var subQ1=sQuery(id+"F0.wireOp",EDGE,"E1.right");Q5=makeQuery(id+"F9.boolean.opBoolean","SPLIT",EDGE,{"disambiguationData":[TD([makeQuery(id+"F1.opExtrude","SWEPT_FACE",FACE,{"disambiguationData":[OSD([subQ1])]})])],"derivedFrom":makeQuery(id+"F9.opExtrude","CAP_EDGE",EDGE,{"disambiguationData":[OSD([subQ0])],"isStart":true})});}
            var Q6;
            {var subQ0=sQuery(id+"F8.wireOp",EDGE,"E9.top");var subQ1=sQuery(id+"F0.wireOp",EDGE,"E1.left");Q6=makeQuery(id+"F9.boolean.opBoolean","SPLIT",EDGE,{"disambiguationData":[TD([makeQuery(id+"F1.opExtrude","SWEPT_FACE",FACE,{"disambiguationData":[OSD([subQ1])]})])],"derivedFrom":makeQuery(id+"F9.opExtrude","CAP_EDGE",EDGE,{"disambiguationData":[OSD([subQ0])],"isStart":true})});}
            fillet(context, id + "F28", {"entities" : qUnion([Q0, Q1, Q2, Q3, Q4, Q5, Q6]), "radius" : 2.54 * mm, "tangentPropagation" : true, "allowEdgeOverflow" : false});
        }
    });
